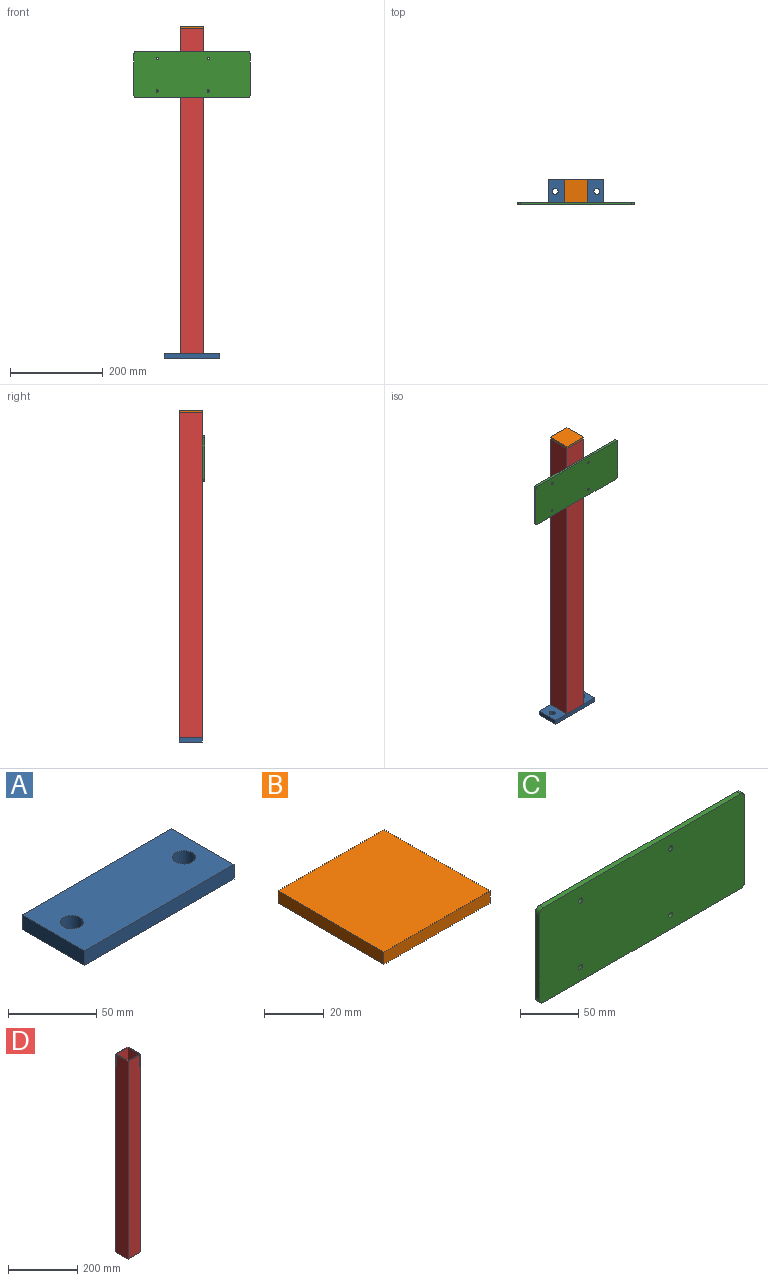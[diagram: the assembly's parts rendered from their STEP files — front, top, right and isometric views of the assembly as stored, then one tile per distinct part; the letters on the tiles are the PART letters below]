
ASSEMBLY  parts=4 mates=3
PART A: 8 faces, bbox 120x50x10 mm
  f0: plane 120x10mm, normal (0,1,0), area 1200mm2, adj f1,f3,f4,f5
  f1: plane 50x10mm, normal (-1,0,0), area 500mm2, adj f0,f2,f4,f5
  f2: plane 120x10mm, normal (0,-1,0), area 1200mm2, adj f1,f3,f4,f5
  f3: plane 50x10mm, normal (1,0,0), area 500mm2, adj f0,f2,f4,f5
  f4: plane 120x50mm, normal (0,0,1), area 5734.5mm2, adj f0,f1,f2,f3,f6,f7
  f5: plane 120x50mm, normal (0,0,-1), area 5734.5mm2, adj f0,f1,f2,f3,f6,f7
  f6: cylinder r=6.5mm len=13mm, axis (0,0,1), area 408.4mm2, adj f4,f5
  f7: cylinder r=6.5mm len=13mm, axis (0,0,1), area 408.4mm2, adj f4,f5
PART B: 6 faces, bbox 50x50x5 mm
  f0: plane 50x5mm, normal (1,0,0), area 250mm2, adj f1,f3,f4,f5
  f1: plane 50x5mm, normal (0,1,0), area 250mm2, adj f0,f2,f4,f5
  f2: plane 50x5mm, normal (-1,0,0), area 250mm2, adj f1,f3,f4,f5
  f3: plane 50x5mm, normal (0,-1,0), area 250mm2, adj f0,f2,f4,f5
  f4: plane 50x50mm, normal (0,0,1), area 2500mm2, adj f0,f1,f2,f3
  f5: plane 50x50mm, normal (0,0,-1), area 2500mm2, adj f0,f1,f2,f3
PART C: 14 faces, bbox 250x5x100 mm
  f0: plane 240x5mm, normal (0,0,1), area 1200mm2, adj f4,f5,f10,f13
  f1: plane 90x5mm, normal (-1,0,0), area 450mm2, adj f4,f5,f10,f11
  f2: plane 240x5mm, normal (0,0,-1), area 1200mm2, adj f4,f5,f11,f12
  f3: plane 90x5mm, normal (1,0,0), area 450mm2, adj f4,f5,f12,f13
  f4: plane 250x100mm, normal (0,-1,0), area 24900mm2, adj f0,f1,f2,f3,f6,f7,f8,f9
  f5: plane 250x100mm, normal (0,1,0), area 24900mm2, adj f0,f1,f2,f3,f6,f7,f8,f9
  f6: cylinder r=2.5mm len=5mm, axis (0,-1,0), area 78.5mm2, adj f4,f5
  f7: cylinder r=2.5mm len=5mm, axis (0,-1,0), area 78.5mm2, adj f4,f5
  f8: cylinder r=2.5mm len=5mm, axis (0,-1,0), area 78.5mm2, adj f4,f5
  f9: cylinder r=2.5mm len=5mm, axis (0,-1,0), area 78.5mm2, adj f4,f5
  f10: cylinder r=5mm len=5mm, axis (0,-1,0), area 39.3mm2, adj f0,f1,f4,f5
  f11: cylinder r=5mm len=5mm, axis (0,1,0), area 39.3mm2, adj f1,f2,f4,f5
  f12: cylinder r=5mm len=5mm, axis (0,-1,0), area 39.3mm2, adj f2,f3,f4,f5
  f13: cylinder r=5mm len=5mm, axis (0,1,0), area 39.3mm2, adj f0,f3,f4,f5
PART D: 10 faces, bbox 50x50x700 mm
  f0: plane 50x50mm, normal (0,0,1), area 475mm2, adj f2,f3,f4,f5,f6,f7,f8,f9
  f1: plane 50x50mm, normal (0,0,-1), area 475mm2, adj f2,f3,f4,f5,f6,f7,f8,f9
  f2: plane 700x50mm, normal (0,1,0), area 35000mm2, adj f0,f1,f3,f5
  f3: plane 700x50mm, normal (-1,0,0), area 35000mm2, adj f0,f1,f2,f4
  f4: plane 700x50mm, normal (0,-1,0), area 35000mm2, adj f0,f1,f3,f5
  f5: plane 700x50mm, normal (1,0,0), area 35000mm2, adj f0,f1,f2,f4
  f6: plane 700x45mm, normal (0,-1,0), area 31500mm2, adj f0,f1,f7,f9
  f7: plane 700x45mm, normal (1,0,0), area 31500mm2, adj f0,f1,f6,f8
  f8: plane 700x45mm, normal (0,1,0), area 31500mm2, adj f0,f1,f7,f9
  f9: plane 700x45mm, normal (-1,0,0), area 31500mm2, adj f0,f1,f6,f8
PLACE A t=(-319.32,-4.12,-47.41)mm
PLACE B t=(-319.32,-4.12,662.59)mm
PLACE C t=(-319.38,-29.12,562.59)mm
PLACE D t=(-319.32,-4.12,-37.41)mm
MATE fastened C.f5 <-> D.f4  axis (0,1,0) through (-319.32,-29.12,562.59)mm
MATE fastened B.f5 <-> D.f0  axis (0,0,-1) through (-344.32,-4.12,662.59)mm
MATE fastened A.f4 <-> D.f1  axis (0,0,1) through (-319.32,-29.12,-37.41)mm
